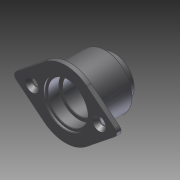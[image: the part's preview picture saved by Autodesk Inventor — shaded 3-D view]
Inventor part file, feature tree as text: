
AUTODESK INVENTOR PART (.ipt)
format: ipt  version: 2014 SP1 (Build 180222100, 222)  size: 144,384 bytes
history: native  units: in
note: dims shown in document units (in); Inventor stores cm internally (conversion verified against a paired STEP export)
features: chamfer x1, other x1, imported_body x1
ambient origin geometry x8: Origin, YZ Plane, XZ Plane, XY Plane, X Axis, Y Axis, Z Axis, Center Point
bodies: Body1 (feature_tree)
feature tree (3):
  chamfer  "Chamfer1"  [1 undecoded]
  other  "217-3422-004 Rev2.ipt1"
  imported_body  "Base1"
note: 1 required parameter value undecoded (feature->parameter linkage not recoverable at this tier; creation-order binding heuristic only, values carry confidence <= 0.55)
